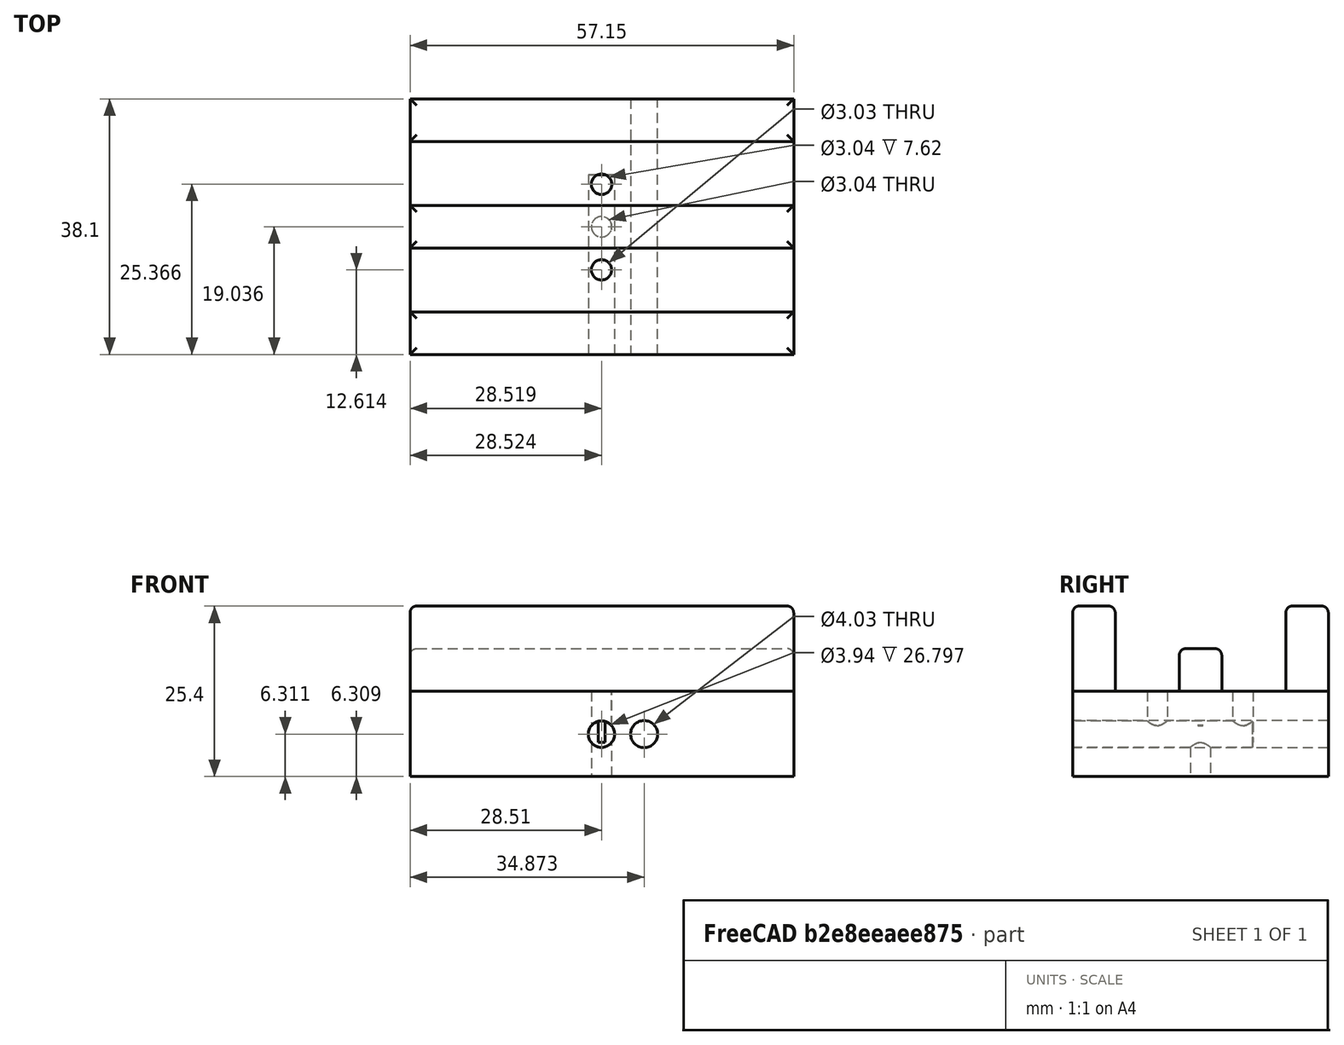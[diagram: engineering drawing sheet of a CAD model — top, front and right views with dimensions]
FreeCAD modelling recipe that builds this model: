
FCSTD DOCUMENT  (FreeCAD 0.15R4671 (Git))
Label: grease_ninja
License: All rights reserved
LicenseURL: http://en.wikipedia.org/wiki/All_rights_reserved
objects: Sketcher::SketchObject×6, PartDesign::Pad×5, Part::Box×4, Part::Fillet×3, Part::Cut×3, Part::MultiFuse×2
note: 28 computed .brp shape members not serialized (recipe doc carries the construction recipe); baked Part::Feature solids carry a one-line shape summary decoded from their .brp

FEATURE [Part::Box] Box  label="Cube"
  Height = 12.7
  Length = 57.15
  Width = 38.1
FEATURE [Part::Box] Box001  label="Cube001"
  Height = 12.7
  Length = 57.15
  Placement = pos=(0,0,12.7) rot=(0,0,1;0rad)
  Width = 6.35
FEATURE [Part::Box] Box002  label="Cube002"
  Height = 12.7
  Length = 57.15
  Placement = pos=(0,31.75,12.7) rot=(0,0,1;0rad)
  Width = 6.35
FEATURE [Part::Box] Box003  label="Cube003"
  Height = 6.35
  Length = 57.15
  Placement = pos=(0,15.875,12.7) rot=(0,0,1;0rad)
  Width = 6.35
FEATURE [Part::Fillet] Fillet
  Base = -> Box001
  Edges = 4 edges r=1: [Edge2,Edge6,Edge10,Edge12]
FEATURE [Part::Fillet] Fillet001
  Base = -> Box002
  Edges = 4 edges r=1: [Edge2,Edge6,Edge10,Edge12]
FEATURE [Part::Fillet] Fillet002
  Base = -> Box003
  Edges = 4 edges r=1: [Edge2,Edge6,Edge10,Edge12]
FEATURE [Sketcher::SketchObject] Sketch
FEATURE [Sketcher::SketchObject] Sketch001
  sketch-geometry (1):
    g0: Circle CenterX=28.5242 CenterY=19.0362 CenterZ=0 NormalX=0 NormalY=0 NormalZ=1 Radius=1.5192
FEATURE [PartDesign::Pad] Pad
  Length = 7.62
  Length2 = 100
  Sketch = -> Sketch001
  Type = 0
FEATURE [Part::Cut] Cut
  Base = -> Box
  Tool = -> Pad
FEATURE [Sketcher::SketchObject] Sketch002
  Placement = pos=(0,0,0) rot=(1,0,0;1.5708rad)
  sketch-geometry (1):
    g0: Circle CenterX=28.5099 CenterY=6.30875 CenterZ=0 NormalX=0 NormalY=0 NormalZ=1 Radius=1.96842
FEATURE [PartDesign::Pad] Pad001
  Length = 26.797
  Length2 = 100
  Placement = pos=(0,0,0) rot=(1,0,0;1.5708rad)
  Reversed = true
  Sketch = -> Sketch002
  Type = 0
FEATURE [Sketcher::SketchObject] Sketch003
  Placement = pos=(0,0,5.08) rot=(0,0,1;0rad)
  sketch-geometry (1):
    g0: Circle CenterX=28.5188 CenterY=12.6142 CenterZ=0 NormalX=0 NormalY=0 NormalZ=1 Radius=1.5136
FEATURE [PartDesign::Pad] Pad002
  Length = 7.62
  Length2 = 100
  Placement = pos=(0,0,5.08) rot=(0,0,1;0rad)
  Sketch = -> Sketch003
  Type = 0
FEATURE [Sketcher::SketchObject] Sketch004
  Placement = pos=(0,0,5.08) rot=(0,0,1;0rad)
  sketch-geometry (1):
    g0: Circle CenterX=28.5237 CenterY=25.3664 CenterZ=0 NormalX=0 NormalY=0 NormalZ=1 Radius=1.52075
FEATURE [PartDesign::Pad] Pad003
  Length = 7.62
  Length2 = 100
  Placement = pos=(0,0,5.08) rot=(0,0,1;0rad)
  Sketch = -> Sketch004
  Type = 0
FEATURE [Part::MultiFuse] Fusion
  Shapes = -> [Pad002,Pad001,Pad003]
FEATURE [Part::MultiFuse] Fusion001
  Shapes = -> [Pad,Fusion]
FEATURE [Part::Cut] Cut001
  Base = -> Cut
  Tool = -> Fusion001
FEATURE [Sketcher::SketchObject] Sketch005
  Placement = pos=(0,0,0) rot=(-1,0,0;4.71239rad)
  sketch-geometry (1):
    g0: Circle CenterX=34.873 CenterY=6.31109 CenterZ=0 NormalX=0 NormalY=0 NormalZ=1 Radius=2.01665
FEATURE [PartDesign::Pad] Pad004
  Length = 38.1
  Length2 = 100
  Placement = pos=(0,0,0) rot=(-1,0,0;4.71239rad)
  Reversed = true
  Sketch = -> Sketch005
  Type = 0
FEATURE [Part::Cut] Cut002
  Base = -> Cut001
  Tool = -> Pad004
